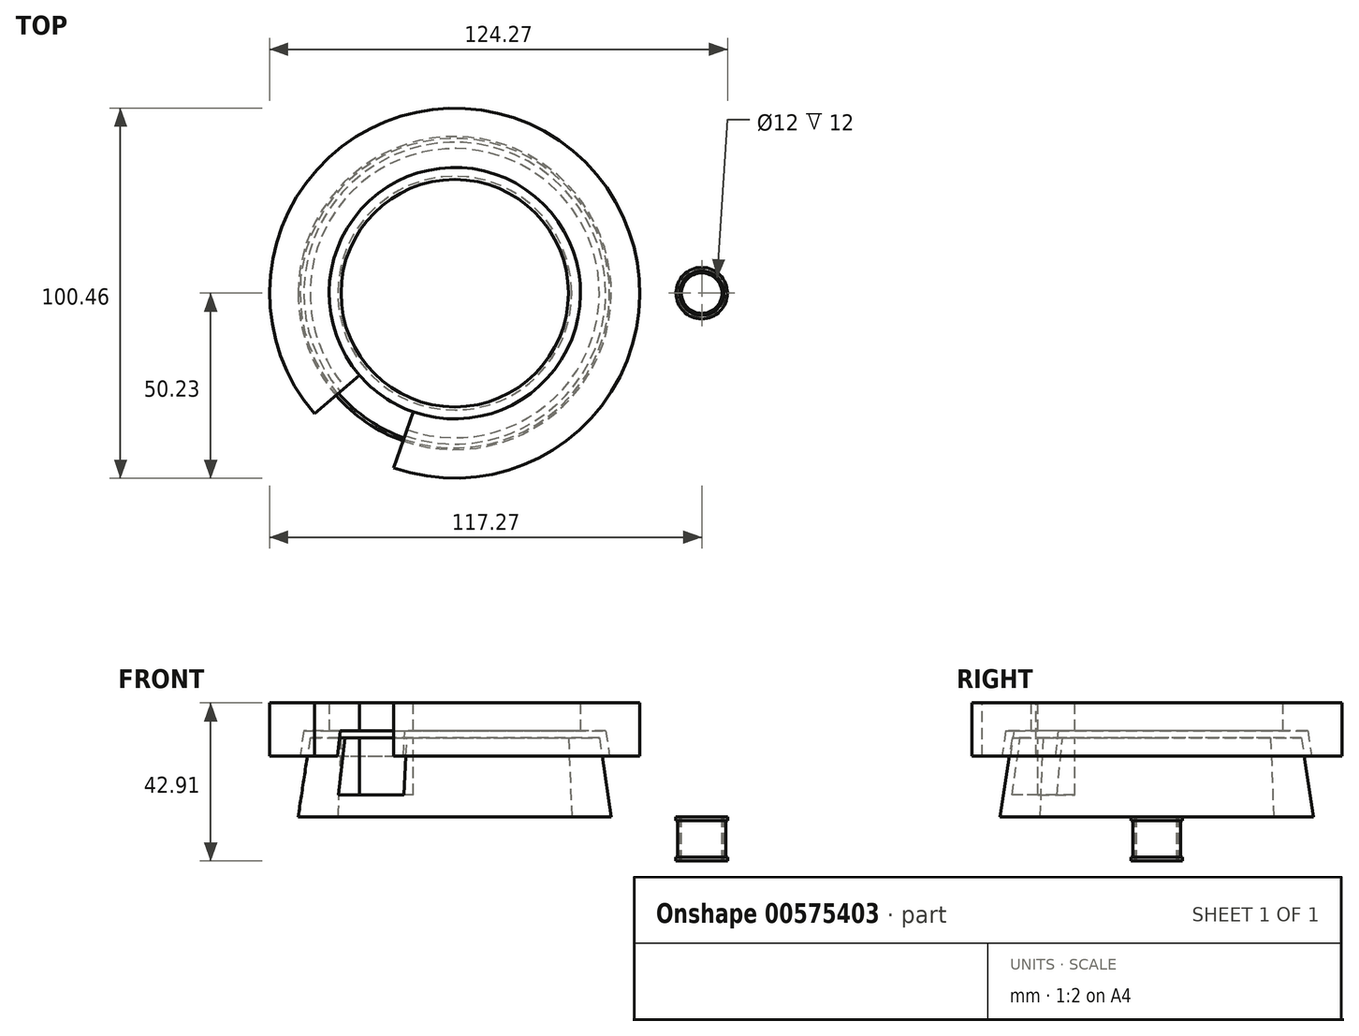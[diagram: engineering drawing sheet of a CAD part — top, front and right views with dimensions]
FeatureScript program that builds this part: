
annotation { "Feature Type Name" : "Feature", "Feature Type Description" : "" }
export const myFeature = defineFeature(function(context is Context, id is Id, definition is map)
    precondition{}
    {
        {
            var Q0;
            Q0=qCreatedBy(makeId("Top.planeOp"),FACE);
            var sketch = newSketch(context, id + "F0", { "sketchPlane" : qUnion([Q0])});
            skCircle(sketch, "E0", {"center": v(0, 0) * mm, "radius": 6 * mm});
            skCircle(sketch, "E1", {"center": v(0, 0) * mm, "radius": 5.5 * mm});
            skCircle(sketch, "E2.0", {"center": v(0, 0) * mm, "radius": 6.5 * mm});
            skCircle(sketch, "E3.0", {"center": v(0, 0) * mm, "radius": 7 * mm});
            skSolve(sketch);
        }
        {
            var Q0;
            Q0=makeQuery(id+"F0.imprint","IMPRINT",FACE,{"disambiguationData":[TD([[makeQuery(id+"F0.imprint","IMPRINT",EDGE,{"derivedFrom":sQuery(id+"F0.wireOp",EDGE,"E0")}),-1.0]])]});
            extrude(context, id + "F1", {"entities" : qUnion([Q0]), "oppositeDirection" : true, "depth" : 6 * mm, "offsetDistance" : 25 * mm});
        }
        {
            var Q0;
            Q0=makeQuery(id+"F0.imprint","IMPRINT",FACE,{"disambiguationData":[TD([[makeQuery(id+"F0.imprint","IMPRINT",EDGE,{"derivedFrom":sQuery(id+"F0.wireOp",EDGE,"E2.0")}),-1.0]])]});
            extrude(context, id + "F2", {"entities" : qUnion([Q0]), "operationType" : NewBodyOperationType.ADD, "oppositeDirection" : true, "depth" : 1 * mm, "offsetDistance" : 25 * mm});
        }
        {
            var Q0;
            Q0=makeQuery(id+"F1.opExtrude","SWEPT_BODY",BODY,{"disambiguationData":[OSD([sQuery(id+"F0.wireOp",EDGE,"E0"),sQuery(id+"F0.wireOp",EDGE,"E2.0")])]});
            var Q1;
            Q1=makeQuery(id+"F1.opExtrude","CAP_FACE",FACE,{"disambiguationData":[OSD([sQuery(id+"F0.wireOp",EDGE,"E0"),sQuery(id+"F0.wireOp",EDGE,"E2.0")])],"isStart":false});
            mirror(context, id + "F3", {"operationType" : NewBodyOperationType.ADD, "entities" : qUnion([Q0]), "mirrorPlane" : qUnion([Q1])});
        }
        {
            var Q0;
            Q0=makeQuery(id+"F0.imprint","IMPRINT",FACE,{"disambiguationData":[TD([[makeQuery(id+"F0.imprint","IMPRINT",EDGE,{"derivedFrom":sQuery(id+"F0.wireOp",EDGE,"E1")}),1.0]])]});
            extrude(context, id + "F4", {"entities" : qUnion([Q0]), "oppositeDirection" : true, "depth" : 12 * mm, "offsetDistance" : 25 * mm});
        }
        {
            var Q0;
            Q0=qCreatedBy(makeId("Front.planeOp"),FACE);
            var sketch = newSketch(context, id + "F5", { "sketchPlane" : qUnion([Q0])});
            skLineSegment(sketch, "E4", {"start": v(-44.54, 0) * mm, "end": v(-89.54, 0) * mm});
            skLineSegment(sketch, "E5", {"start": v(-67.04, 0) * mm, "end": v(-67.04, 30) * mm});
            skLineSegment(sketch, "E6", {"start": v(-89.54, 0) * mm, "end": v(-89.54, 21.36) * mm});
            skLineSegment(sketch, "E7", {"start": v(-89.54, 0) * mm, "end": v(-109.54, 0) * mm});
            skLineSegment(sketch, "E8", {"start": v(-109.54, 0) * mm, "end": v(-106.3, 21.36) * mm});
            skLineSegment(sketch, "E9", {"start": v(-89.54, 21.36) * mm, "end": v(-106.3, 21.36) * mm});
            skLineSegment(sketch, "E10.0", {"start": v(-111.52, 0.3) * mm, "end": v(-108.27, 21.66) * mm});
            skLineSegment(sketch, "E11.0", {"start": v(-101.17, 23.36) * mm, "end": v(-106.3, 23.36) * mm});
            skLineSegment(sketch, "E12", {"start": v(-109.06, 16.48) * mm, "end": v(-117.27, 16.48) * mm});
            skLineSegment(sketch, "E13", {"start": v(-117.27, 16.48) * mm, "end": v(-117.27, 30.91) * mm});
            skLineSegment(sketch, "E14", {"start": v(-117.27, 30.91) * mm, "end": v(-101.17, 30.91) * mm});
            skLineSegment(sketch, "E15", {"start": v(-106.3, 23.36) * mm, "end": v(-108.01, 23.36) * mm});
            skLineSegment(sketch, "E16", {"start": v(-108.27, 21.66) * mm, "end": v(-108.01, 23.36) * mm});
            skLineSegment(sketch, "E17", {"start": v(-101.17, 23.36) * mm, "end": v(-101.17, 30.91) * mm});
            skPoint(sketch, "E18.start.orphan", {"position": v(-89.54, 30.91) * mm});
            skPoint(sketch, "E19.orphan", {"position": v(-89.54, 23.36) * mm});
            skLineSegment(sketch, "E20", {"start": v(-97.92, 21.36) * mm, "end": v(-98.78, 0) * mm});
            skSolve(sketch);
        }
        {
            var Q0;
            {var subQ0=sQuery(id+"F5.wireOp",EDGE,"E8");Q0=makeQuery(id+"F5.imprint","IMPRINT",FACE,{"disambiguationData":[TD([[makeQuery(id+"F5.imprint","IMPRINT",EDGE,{"derivedFrom":subQ0}),-1.0]])]});}
            var Q1;
            Q1=sQuery(id+"F5.wireOp",EDGE,"E5");
            revolve(context, id + "F6", {"surfaceOperationType" : NewSurfaceOperationType.NEW, "entities" : qUnion([Q0]), "axis" : qUnion([Q1]), "revolveType" : RevolveType.FULL});
        }
        {
            var Q0;
            Q0=makeQuery(id+"F5.imprint","IMPRINT",FACE,{"disambiguationData":[TD([[makeQuery(id+"F5.imprint","IMPRINT",EDGE,{"derivedFrom":sQuery(id+"F5.wireOp",EDGE,"E11.0")}),-1.0]])]});
            var Q1;
            Q1=sQuery(id+"F5.wireOp",EDGE,"E5");
            revolve(context, id + "F7", {"surfaceOperationType" : NewSurfaceOperationType.NEW, "entities" : qUnion([Q0]), "axis" : qUnion([Q1]), "revolveType" : RevolveType.FULL});
        }
        {
            var Q0;
            Q0=makeQuery(id+"F7.opRevolve","SWEPT_FACE",FACE,{"disambiguationData":[OSD([sQuery(id+"F5.wireOp",EDGE,"E14")])]});
            var sketch = newSketch(context, id + "F8", { "sketchPlane" : qUnion([Q0])});
            skLineSegment(sketch, "E21", {"start": v(-67.04, 0) * mm, "end": v(-105.14, -32.74) * mm});
            skLineSegment(sketch, "E22", {"start": v(-67.04, 0) * mm, "end": v(-83.66, -47.4) * mm});
            skCircle(sketch, "E23", {"center": v(-67.04, 0) * mm, "radius": 50.23 * mm});
            skSolve(sketch);
        }
        {
            var Q0;
            {var subQ0=sQuery(id+"F8.wireOp",EDGE,"E23");var subQ1=sQuery(id+"F8.wireOp",EDGE,"E21");var subQ2=makeQuery(id+"F8.imprint","INTERSECT",VERTEX,{"derivedFrom":[subQ1,subQ0]});Q0=makeQuery(id+"F8.imprint","IMPRINT",FACE,{"disambiguationData":[TD([[makeQuery(id+"F8.imprint","IMPRINT",EDGE,{"disambiguationData":[TD([[subQ2,1.0]])],"derivedFrom":subQ0}),-1.0]])]});}
            extrude(context, id + "F9", {"entities" : qUnion([Q0]), "operationType" : NewBodyOperationType.REMOVE, "oppositeDirection" : true, "depth" : 25 * mm, "offsetDistance" : 25 * mm});
        }
    });
